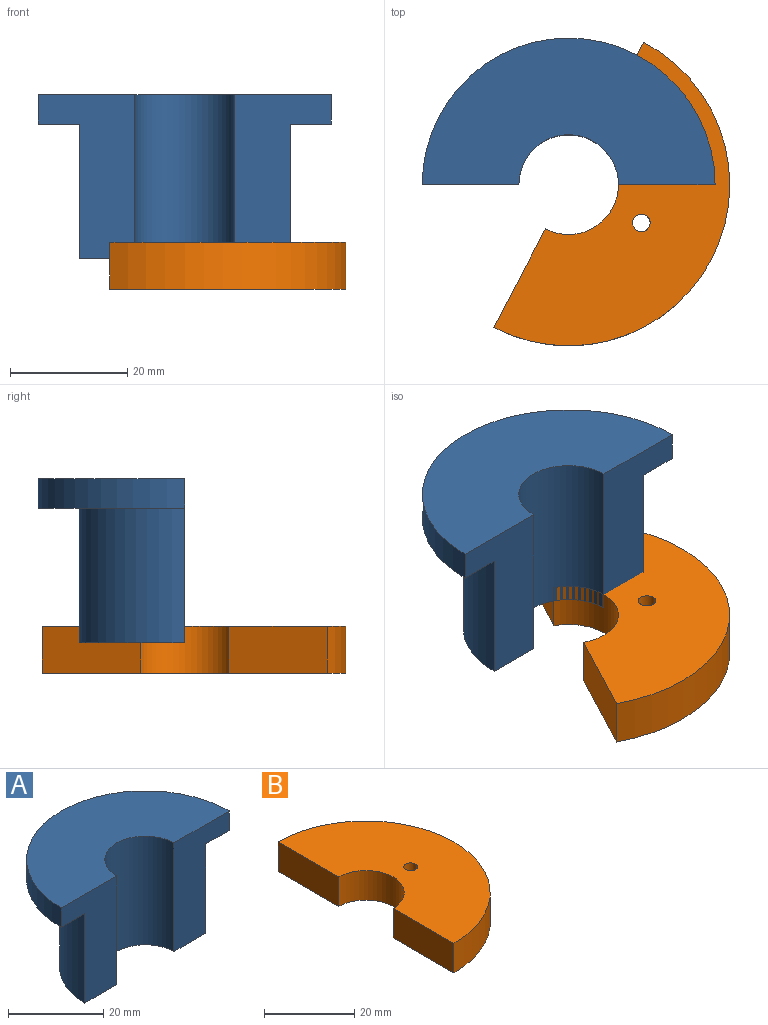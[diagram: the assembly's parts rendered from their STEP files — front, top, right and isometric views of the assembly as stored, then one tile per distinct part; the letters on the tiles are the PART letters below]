
ASSEMBLY  parts=2 mates=1
PART A: 10 faces, bbox 50x25x28 mm
  f0: plane 36x18mm, normal (0,0,-1), area 388.4mm2, adj f1,f2,f3,f8,f9
  f1: cylinder r=1.5mm len=15mm, axis (0,0,1), area 141.4mm2, adj f0,f7
  f2: cylinder r=8.5mm len=28mm, axis (0,0,-1), area 747.7mm2, adj f0,f5,f8,f9
  f3: cylinder r=18mm len=36mm, axis (0,0,-1), area 1300.6mm2, adj f0,f6,f8,f9
  f4: cylinder r=25mm len=50mm, axis (0,0,-1), area 392.7mm2, adj f5,f6,f8,f9
  f5: plane 50x25mm, normal (0,0,1), area 868.3mm2, adj f2,f4,f8,f9
  f6: plane 50x25mm, normal (0,0,-1), area 472.8mm2, adj f3,f4,f8,f9
  f7: plane 3x3mm, normal (0,0,-1), area 7.1mm2, adj f1
  f8: plane 28x16.5mm, normal (0,-1,0), area 301mm2, adj f0,f2,f3,f4,f5,f6
  f9: plane 28x16.5mm, normal (0,-1,0), area 301mm2, adj f0,f2,f3,f4,f5,f6
PART B: 7 faces, bbox 27.5x55x8 mm
  f0: plane 55x27.5mm, normal (0,0,-1), area 1067.4mm2, adj f1,f2,f4,f5,f6
  f1: cylinder r=8.5mm len=17mm, axis (0,0,-1), area 213.6mm2, adj f0,f3,f5,f6
  f2: cylinder r=27.5mm len=55mm, axis (0,0,-1), area 691.2mm2, adj f0,f3,f5,f6
  f3: plane 55x27.5mm, normal (0,0,1), area 1067.4mm2, adj f1,f2,f4,f5,f6
  f4: cylinder r=1.5mm len=8mm, axis (0,0,-1), area 75.4mm2, adj f0,f3
  f5: plane 19x8mm, normal (-1,0,0), area 152mm2, adj f0,f1,f2,f3
  f6: plane 19x8mm, normal (-1,0,0), area 152mm2, adj f0,f1,f2,f3
PLACE A at identity fixed
PLACE B rot(axis=(0,0,-1),27.7deg) t=(0,0,-5.21)mm
MATE cylindrical B.f2 <-> A.f3  axis (0,0,-1) through (0,0,-1.21)mm
